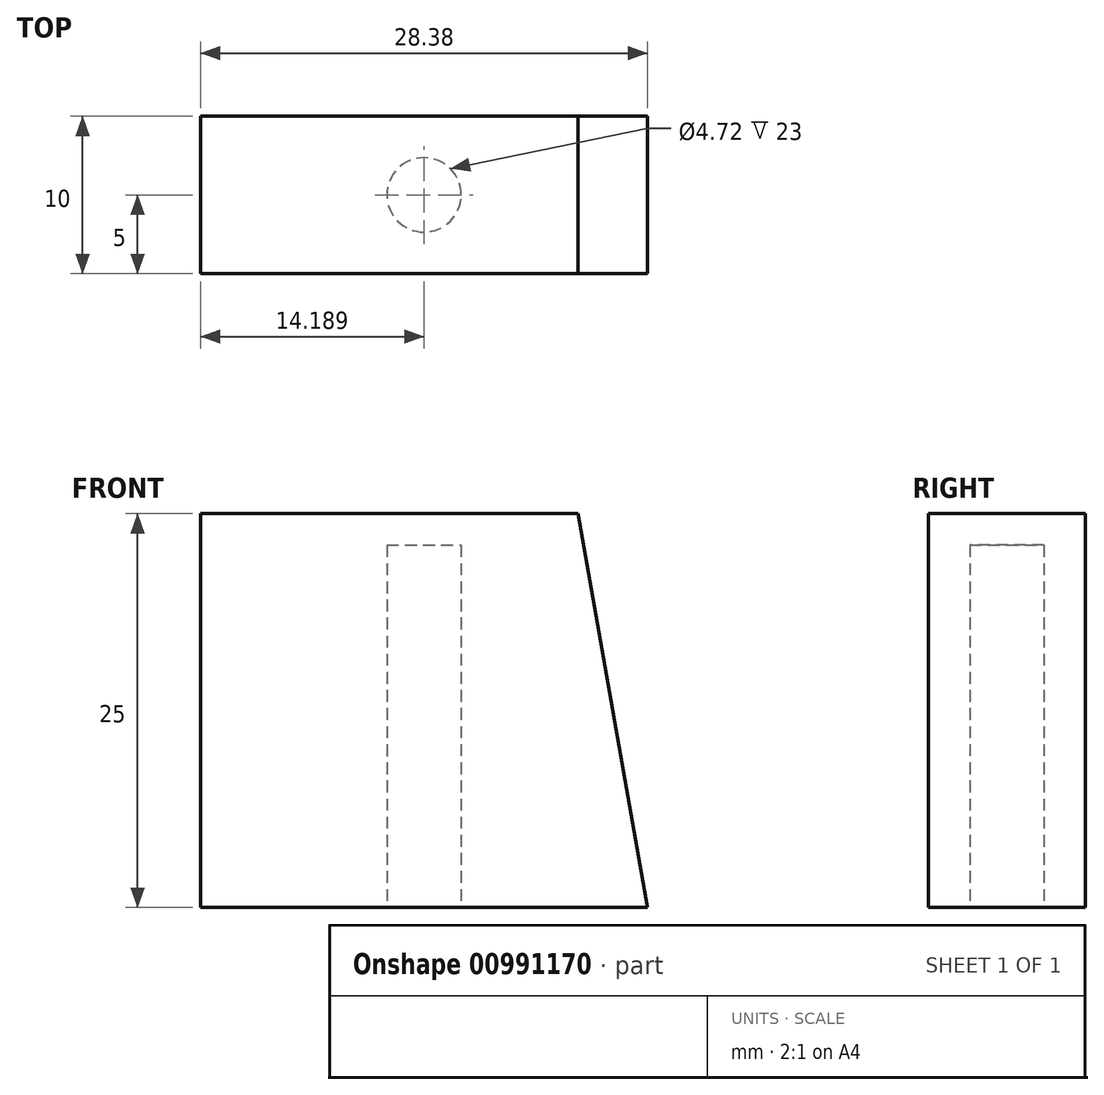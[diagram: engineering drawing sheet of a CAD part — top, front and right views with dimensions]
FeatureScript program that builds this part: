
annotation { "Feature Type Name" : "Feature", "Feature Type Description" : "" }
export const myFeature = defineFeature(function(context is Context, id is Id, definition is map)
    precondition{}
    {
        {
            var Q0;
            Q0=qCreatedBy(makeId("Front.planeOp"),FACE);
            var sketch = newSketch(context, id + "F0", { "sketchPlane" : qUnion([Q0])});
            skLineSegment(sketch, "E0", {"start": v(0, 0) * mm, "end": v(0, 25) * mm});
            skLineSegment(sketch, "E1", {"start": v(0, 25) * mm, "end": v(23.97, 25) * mm});
            skLineSegment(sketch, "E2", {"start": v(23.97, 25) * mm, "end": v(28.38, 0) * mm});
            skLineSegment(sketch, "E3", {"start": v(28.38, 0) * mm, "end": v(0, 0) * mm});
            skSolve(sketch);
        }
        {
            var Q0;
            Q0=makeQuery(id+"F0.imprint","IMPRINT",FACE,{"disambiguationData":[TD([[makeQuery(id+"F0.imprint","IMPRINT",EDGE,{"derivedFrom":sQuery(id+"F0.wireOp",EDGE,"E0")}),-1.0]])]});
            extrude(context, id + "F1", {"entities" : qUnion([Q0]), "oppositeDirection" : true, "depth" : 10 * mm, "offsetDistance" : 25 * mm});
        }
        {
            var Q0;
            Q0=makeQuery(id+"F1.opExtrude","SWEPT_FACE",FACE,{"disambiguationData":[OSD([sQuery(id+"F0.wireOp",EDGE,"E3")])]});
            var sketch = newSketch(context, id + "F2", { "sketchPlane" : qUnion([Q0])});
            skCircle(sketch, "E4", {"center": v(14.19, -5) * mm, "radius": 2.36 * mm});
            skPoint(sketch, "E4.centerSnap0", {"position": v(0, -5) * mm});
            skPoint(sketch, "E4.centerSnap1", {"position": v(14.19, -10) * mm});
            skSolve(sketch);
        }
        {
            var Q0;
            Q0=makeQuery(id+"F2.imprint","IMPRINT",FACE,{"disambiguationData":[TD([[makeQuery(id+"F2.imprint","IMPRINT",EDGE,{"derivedFrom":sQuery(id+"F2.wireOp",EDGE,"E4")}),1.0]])]});
            extrude(context, id + "F3", {"entities" : qUnion([Q0]), "operationType" : NewBodyOperationType.REMOVE, "oppositeDirection" : true, "depth" : 23 * mm, "offsetDistance" : 25 * mm});
        }
    });
